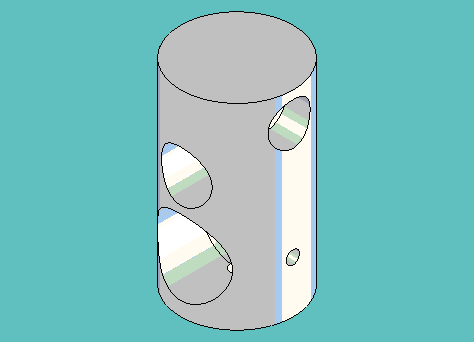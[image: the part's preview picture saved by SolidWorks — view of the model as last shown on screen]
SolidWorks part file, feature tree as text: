
SOLIDWORKS PART (.sldprt)
format: sldprt  version: not decoded by parser v0  size: 430,592 bytes
history: native  units: mm
features: sketch x8, extrude x5, boolean_combine x5, revolve x2, material x1, cut_extrude x1, plane x1 (+11 scaffold rows collapsed)
feature tree (34):
  scaffold x11  (default folders/planes/origin — collapsed)
  material  "Material <not specified>"
  sketch  "Sketch1"  dims[D1=33.3375mm D2=9.525mm D3=153.9875mm]
  revolve  "Revolve1"  Angle=360deg
  sketch  "Sketch2"  dims[c1.D1=3.4544mm c1.D2=2.2606mm c1.D3=8.7376mm c1.D4=28.3464mm c2.D3=8.7376mm c2.D4=28.3464mm]
  extrude  "Extrude1"  [1 undecoded]
  boolean_combine  "Combine1"
  sketch  "Sketch3"  dims[D1=2.2606mm]
  extrude  "Extrude2"  Depth=7.9756mm
  sketch  "Sketch5"  dims[c1.D4=~4.437453mm c1.D5=6.35mm c1.D1=8.7376mm c1.D2=6.35mm c1.D3=6.35mm c2.D4=9.525mm c2.D2=9.525mm c3.D4=9.525mm c3.D6=12.7mm c4.D4=3.175mm]
  revolve  "Revolve2"  Angle=360deg
  boolean_combine  "Combine4"
  sketch  "Sketch11"  dims[D1=~10.31875mm]
  cut_extrude  "Cut-Extrude1"  Depth=177.8mm
  boolean_combine  "Combine5"
  sketch  "Sketch6"  dims[D1=8.5852mm D2=20.6502mm]
  extrude  "Extrude3"  [1 undecoded]
  boolean_combine  "Combine6"
  sketch  "Sketch9"  dims[c1.D1=4.3688mm c1.D2=2.2606mm c1.D3=8.7376mm c1.D4=28.3464mm c2.D3=8.7376mm c2.D4=28.3464mm]
  extrude  "Extrude5"  [1 undecoded]
  plane  "Plane1"  Offset=12.7mm
  sketch  "Sketch10"  dims[D1=~7.14375mm]
  extrude  "Extrude6"  Depth=7.9375mm
  boolean_combine  "Combine7"
decode coverage: 13 of 21 modeling features carry decoded parameters
note: ~ marks probable driven/reference dimensions
note: 3 parameter values undecoded
summary: no parameter record found for 3 features
note: suppression state not decoded; provenance and decode notes live in map.json
